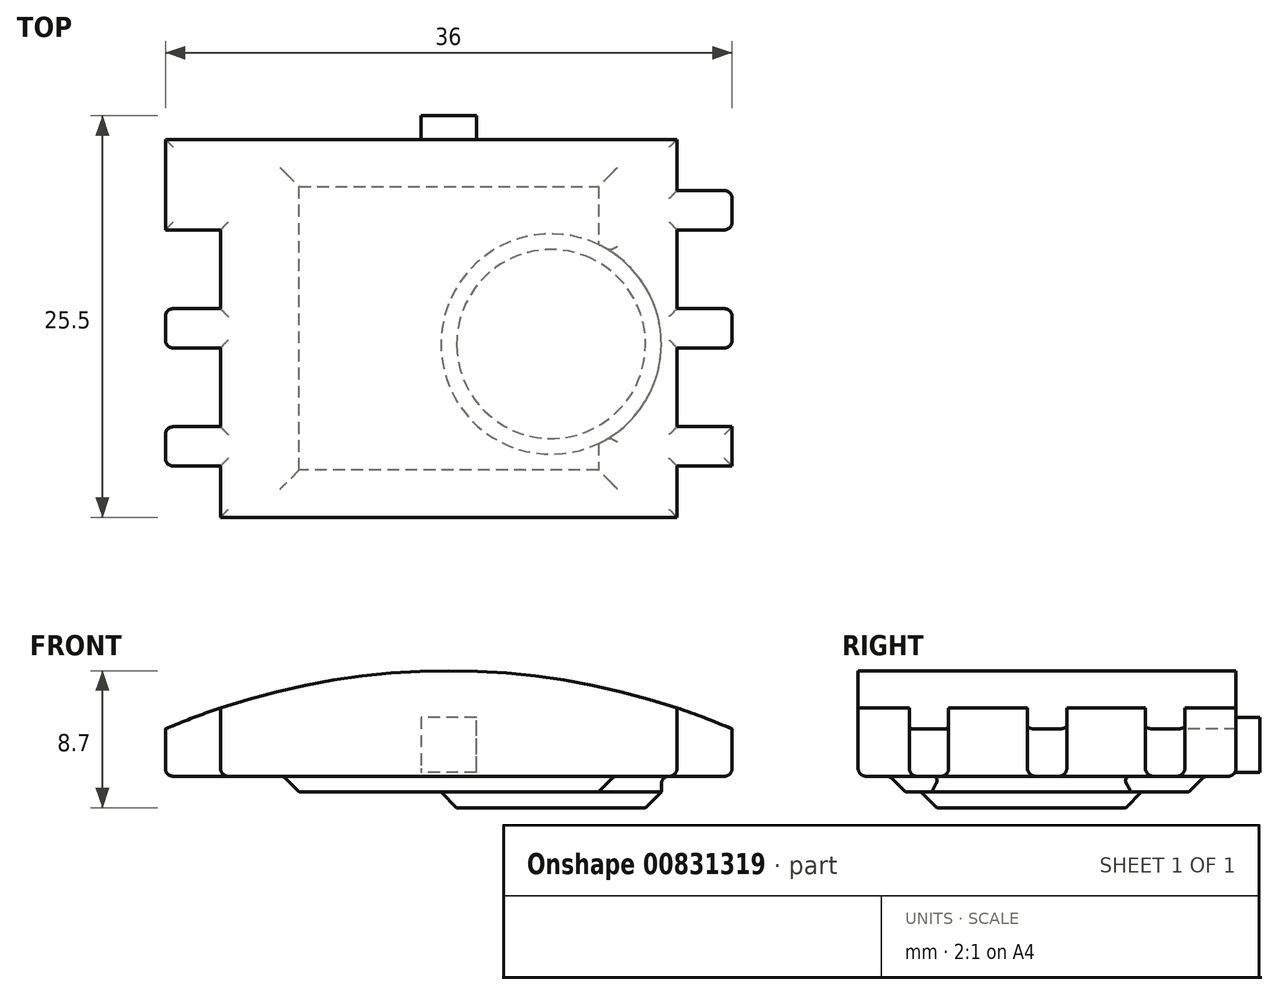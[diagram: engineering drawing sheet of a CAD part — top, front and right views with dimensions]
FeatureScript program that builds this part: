
annotation { "Feature Type Name" : "Feature", "Feature Type Description" : "" }
export const myFeature = defineFeature(function(context is Context, id is Id, definition is map)
    precondition{}
    {
        {
            var Q0;
            Q0=qCreatedBy(makeId("Top.planeOp"),FACE);
            var sketch = newSketch(context, id + "F0", { "sketchPlane" : qUnion([Q0])});
            skLineSegment(sketch, "E0.bottom", {"start": v(18, 12) * mm, "end": v(-18, 12) * mm});
            skLineSegment(sketch, "E0.top", {"start": v(18, -12) * mm, "end": v(-18, -12) * mm});
            skLineSegment(sketch, "E0.left", {"start": v(18, 12) * mm, "end": v(18, -12) * mm});
            skLineSegment(sketch, "E0.right", {"start": v(-18, 12) * mm, "end": v(-18, -12) * mm});
            skPoint(sketch, "E0.middle", {"position": v(0, 0) * mm});
            skSolve(sketch);
        }
        {
            var Q0;
            Q0=makeQuery(id+"F0.imprint","IMPRINT",FACE,{"disambiguationData":[TD([[makeQuery(id+"F0.imprint","IMPRINT",EDGE,{"derivedFrom":sQuery(id+"F0.wireOp",EDGE,"E0.bottom")}),1.0]])]});
            extrude(context, id + "F1", {"entities" : qUnion([Q0]), "depth" : 6.7 * mm, "offsetDistance" : 25 * mm});
        }
        {
            var Q0;
            Q0=makeQuery(id+"F1.opExtrude","SWEPT_FACE",FACE,{"disambiguationData":[OSD([sQuery(id+"F0.wireOp",EDGE,"E0.top")])]});
            var sketch = newSketch(context, id + "F2", { "sketchPlane" : qUnion([Q0])});
            skLineSegment(sketch, "E1", {"start": v(-18, 0) * mm, "end": v(-18, 3) * mm});
            skLineSegment(sketch, "E2.top", {"start": v(-18, 0) * mm, "end": v(18, 0) * mm});
            skLineSegment(sketch, "E2.left", {"start": v(-18, 3) * mm, "end": v(-18, 0) * mm});
            skLineSegment(sketch, "E2.right", {"start": v(18, 4.65) * mm, "end": v(18, 0) * mm});
            skLineSegment(sketch, "E3.bottom", {"start": v(-18, 3) * mm, "end": v(18, 3) * mm});
            skLineSegment(sketch, "E3.right", {"start": v(18, 3) * mm, "end": v(18, 0) * mm});
            skLineSegment(sketch, "E4", {"start": v(0, 3) * mm, "end": v(0, 6.7) * mm});
            skArc(sketch, "E5", {"start": v(18, 3) * mm, "mid": v(0, 6.7) * mm, "end": v(-18, 3) * mm});
            skSolve(sketch);
        }
        {
            var Q0;
            Q0=makeQuery(id+"F2.imprint","IMPRINT",FACE,{"disambiguationData":[TD([[makeQuery(id+"F2.imprint","IMPRINT",EDGE,{"derivedFrom":sQuery(id+"F2.wireOp",EDGE,"E2.top")}),-1.0]])]});
            var Q1;
            {var subQ4=sQuery(id+"F2.wireOp",EDGE,"E4");Q1=makeQuery(id+"F2.imprint","IMPRINT",FACE,{"disambiguationData":[TD([[makeQuery(id+"F2.imprint","IMPRINT",EDGE,{"derivedFrom":subQ4}),1.0]])]});}
            var Q2;
            {var subQ3=sQuery(id+"F2.wireOp",EDGE,"E4");Q2=makeQuery(id+"F2.imprint","IMPRINT",FACE,{"disambiguationData":[TD([[makeQuery(id+"F2.imprint","IMPRINT",EDGE,{"derivedFrom":subQ3}),-1.0]])]});}
            var Q3;
            Q3=makeQuery(id+"F2.imprint","IMPRINT",FACE,{"disambiguationData":[TD([[makeQuery(id+"F2.imprint","IMPRINT",EDGE,{"derivedFrom":sQuery(id+"F2.wireOp",EDGE,"E2.top")}),-1.0]])]});
            extrude(context, id + "F3", {"entities" : qUnion([Q0, Q1, Q2, Q3]), "operationType" : NewBodyOperationType.INTERSECT, "oppositeDirection" : true, "depth" : 50 * mm, "offsetDistance" : 25 * mm});
        }
        {
            var Q0;
            Q0=makeQuery(id+"F1.opExtrude","SWEPT_FACE",FACE,{"disambiguationData":[OSD([sQuery(id+"F0.wireOp",EDGE,"E0.bottom")])]});
            var sketch = newSketch(context, id + "F4", { "sketchPlane" : qUnion([Q0])});
            skLineSegment(sketch, "E6", {"start": v(0, 0) * mm, "end": v(0, 2) * mm});
            skPoint(sketch, "E7.0.midPoint", {"position": v(0, 0) * mm});
            skCircle(sketch, "E8.cCircle", {"center": v(0, 2) * mm, "radius": 1.75 * mm, "construction": true});
            skLineSegment(sketch, "E8.0", {"start": v(1.75, 0.25) * mm, "end": v(-1.75, 0.25) * mm});
            skLineSegment(sketch, "E8.1", {"start": v(-1.75, 0.25) * mm, "end": v(-1.75, 3.75) * mm});
            skLineSegment(sketch, "E8.2", {"start": v(-1.75, 3.75) * mm, "end": v(1.75, 3.75) * mm});
            skLineSegment(sketch, "E8.3", {"start": v(1.75, 3.75) * mm, "end": v(1.75, 0.25) * mm});
            skPoint(sketch, "E8.0.midPoint", {"position": v(0, 0.25) * mm});
            skSolve(sketch);
        }
        {
            var Q0;
            {var subQ0=sQuery(id+"F4.wireOp",EDGE,"E8.1");Q0=makeQuery(id+"F4.imprint","IMPRINT",FACE,{"disambiguationData":[TD([[makeQuery(id+"F4.imprint","IMPRINT",EDGE,{"derivedFrom":subQ0}),-1.0]])]});}
            extrude(context, id + "F5", {"entities" : qUnion([Q0]), "operationType" : NewBodyOperationType.ADD, "depth" : 1.5 * mm, "offsetDistance" : 25 * mm});
        }
        {
            var Q0;
            Q0=makeQuery(id+"F1.opExtrude","CAP_FACE",FACE,{"disambiguationData":[OSD([sQuery(id+"F0.wireOp",EDGE,"E0.bottom"),sQuery(id+"F0.wireOp",EDGE,"E0.top"),sQuery(id+"F0.wireOp",EDGE,"E0.left"),sQuery(id+"F0.wireOp",EDGE,"E0.right")])],"isStart":true});
            var sketch = newSketch(context, id + "F6", { "sketchPlane" : qUnion([Q0])});
            skLineSegment(sketch, "E9.bottom", {"start": v(-10.5, 10) * mm, "end": v(10.5, 10) * mm});
            skLineSegment(sketch, "E9.top", {"start": v(-10.5, -10) * mm, "end": v(10.5, -10) * mm});
            skLineSegment(sketch, "E9.left", {"start": v(-10.5, 10) * mm, "end": v(-10.5, -10) * mm});
            skLineSegment(sketch, "E9.right", {"start": v(10.5, 10) * mm, "end": v(10.5, -10) * mm});
            skLineSegment(sketch, "E10", {"start": v(-18, -12) * mm, "end": v(-18, -8.75) * mm});
            skLineSegment(sketch, "E11", {"start": v(-18, -8.75) * mm, "end": v(-18, -6.25) * mm});
            skLineSegment(sketch, "E12", {"start": v(-18, -6.25) * mm, "end": v(-18, -1.25) * mm});
            skLineSegment(sketch, "E13", {"start": v(-18, -1.25) * mm, "end": v(-18, 1.25) * mm});
            skLineSegment(sketch, "E14", {"start": v(-18, 1.25) * mm, "end": v(-18, 6.25) * mm});
            skLineSegment(sketch, "E15", {"start": v(-18, 6.25) * mm, "end": v(-18, 8.75) * mm});
            skLineSegment(sketch, "E16", {"start": v(-18, 8.75) * mm, "end": v(-18, 12) * mm});
            skLineSegment(sketch, "E17", {"start": v(-18, -12) * mm, "end": v(-14.5, -12) * mm});
            skLineSegment(sketch, "E18.bottom", {"start": v(-14.5, -12) * mm, "end": v(-18, -12) * mm});
            skLineSegment(sketch, "E18.top", {"start": v(-14.5, -8.75) * mm, "end": v(-18, -8.75) * mm});
            skLineSegment(sketch, "E18.left", {"start": v(-14.5, -12) * mm, "end": v(-14.5, -8.75) * mm});
            skLineSegment(sketch, "E19.top", {"start": v(-14.5, -6.25) * mm, "end": v(-18, -6.25) * mm});
            skLineSegment(sketch, "E19.left", {"start": v(-14.5, -8.75) * mm, "end": v(-14.5, -6.25) * mm});
            skLineSegment(sketch, "E20.top", {"start": v(-14.5, -1.25) * mm, "end": v(-18, -1.25) * mm});
            skLineSegment(sketch, "E20.left", {"start": v(-14.5, -6.25) * mm, "end": v(-14.5, -1.25) * mm});
            skLineSegment(sketch, "E21.top", {"start": v(-14.5, 1.25) * mm, "end": v(-18, 1.25) * mm});
            skLineSegment(sketch, "E21.left", {"start": v(-14.5, -1.25) * mm, "end": v(-14.5, 1.25) * mm});
            skLineSegment(sketch, "E22.top", {"start": v(-14.5, 6.25) * mm, "end": v(-18, 6.25) * mm});
            skLineSegment(sketch, "E22.left", {"start": v(-14.5, 1.25) * mm, "end": v(-14.5, 6.25) * mm});
            skLineSegment(sketch, "E23.top", {"start": v(-14.5, 8.75) * mm, "end": v(-18, 8.75) * mm});
            skLineSegment(sketch, "E23.left", {"start": v(-14.5, 6.25) * mm, "end": v(-14.5, 8.75) * mm});
            skLineSegment(sketch, "E24.top", {"start": v(-14.5, 12) * mm, "end": v(-18, 12) * mm});
            skLineSegment(sketch, "E24.left", {"start": v(-14.5, 8.75) * mm, "end": v(-14.5, 12) * mm});
            skLineSegment(sketch, "E25.bottom", {"start": v(18, -12) * mm, "end": v(14.5, -12) * mm});
            skLineSegment(sketch, "E25.top", {"start": v(18, -8.75) * mm, "end": v(14.5, -8.75) * mm});
            skLineSegment(sketch, "E25.left", {"start": v(18, -12) * mm, "end": v(18, -8.75) * mm});
            skLineSegment(sketch, "E25.right", {"start": v(14.5, -12) * mm, "end": v(14.5, -8.75) * mm});
            skLineSegment(sketch, "E26", {"start": v(14.5, -8.75) * mm, "end": v(14.5, -6.25) * mm});
            skLineSegment(sketch, "E27", {"start": v(14.5, -6.25) * mm, "end": v(14.5, -1.25) * mm});
            skLineSegment(sketch, "E28", {"start": v(14.5, -1.25) * mm, "end": v(14.5, 1.25) * mm});
            skLineSegment(sketch, "E29", {"start": v(14.5, 1.25) * mm, "end": v(14.5, 6.25) * mm});
            skLineSegment(sketch, "E30", {"start": v(14.5, 6.25) * mm, "end": v(14.5, 8.75) * mm});
            skLineSegment(sketch, "E31", {"start": v(14.5, 8.75) * mm, "end": v(14.5, 12) * mm});
            skLineSegment(sketch, "E32", {"start": v(14.5, -12) * mm, "end": v(18, -12) * mm});
            skLineSegment(sketch, "E33.top", {"start": v(18, -6.25) * mm, "end": v(14.5, -6.25) * mm});
            skLineSegment(sketch, "E33.left", {"start": v(18, -8.75) * mm, "end": v(18, -6.25) * mm});
            skLineSegment(sketch, "E34.top", {"start": v(18, -1.25) * mm, "end": v(14.5, -1.25) * mm});
            skLineSegment(sketch, "E34.left", {"start": v(18, -6.25) * mm, "end": v(18, -1.25) * mm});
            skLineSegment(sketch, "E35.top", {"start": v(18, 1.25) * mm, "end": v(14.5, 1.25) * mm});
            skLineSegment(sketch, "E35.left", {"start": v(18, -1.25) * mm, "end": v(18, 1.25) * mm});
            skLineSegment(sketch, "E36.top", {"start": v(18, 6.25) * mm, "end": v(14.5, 6.25) * mm});
            skLineSegment(sketch, "E36.left", {"start": v(18, 1.25) * mm, "end": v(18, 6.25) * mm});
            skLineSegment(sketch, "E37.top", {"start": v(18, 8.75) * mm, "end": v(14.5, 8.75) * mm});
            skLineSegment(sketch, "E37.left", {"start": v(18, 6.25) * mm, "end": v(18, 8.75) * mm});
            skLineSegment(sketch, "E38.top", {"start": v(18, 12) * mm, "end": v(14.5, 12) * mm});
            skLineSegment(sketch, "E38.left", {"start": v(18, 8.75) * mm, "end": v(18, 12) * mm});
            skSolve(sketch);
        }
        {
            var Q0;
            Q0=makeQuery(id+"F6.imprint","IMPRINT",FACE,{"disambiguationData":[TD([[makeQuery(id+"F6.imprint","IMPRINT",EDGE,{"derivedFrom":sQuery(id+"F6.wireOp",EDGE,"E9.bottom")}),-1.0]])]});
            extrude(context, id + "F7", {"entities" : qUnion([Q0]), "operationType" : NewBodyOperationType.ADD, "depth" : 1 * mm, "offsetDistance" : 25 * mm});
        }
        {
            var Q0;
            Q0=makeQuery(id+"F7.opExtrude","CAP_EDGE",EDGE,{"disambiguationData":[OSD([sQuery(id+"F6.wireOp",EDGE,"E9.left")])],"isStart":false});
            var Q1;
            Q1=makeQuery(id+"F7.opExtrude","CAP_EDGE",EDGE,{"disambiguationData":[OSD([sQuery(id+"F6.wireOp",EDGE,"E9.bottom")])],"isStart":false});
            var Q2;
            Q2=makeQuery(id+"F7.opExtrude","CAP_EDGE",EDGE,{"disambiguationData":[OSD([sQuery(id+"F6.wireOp",EDGE,"E9.right")])],"isStart":false});
            var Q3;
            Q3=makeQuery(id+"F7.opExtrude","CAP_EDGE",EDGE,{"disambiguationData":[OSD([sQuery(id+"F6.wireOp",EDGE,"E9.top")])],"isStart":false});
            chamfer(context, id + "F8", {"entities" : qUnion([Q0, Q1, Q2, Q3]), "width" : 1 * mm, "tangentPropagation" : true});
        }
        {
            var Q0;
            Q0=makeQuery(id+"F1.opExtrude","CAP_FACE",FACE,{"disambiguationData":[OSD([sQuery(id+"F0.wireOp",EDGE,"E0.bottom"),sQuery(id+"F0.wireOp",EDGE,"E0.top"),sQuery(id+"F0.wireOp",EDGE,"E0.left"),sQuery(id+"F0.wireOp",EDGE,"E0.right")])],"isStart":true});
            var sketch = newSketch(context, id + "F9", { "sketchPlane" : qUnion([Q0])});
            skLineSegment(sketch, "E39.bottom", {"start": v(18, 12) * mm, "end": v(6.5, 12) * mm});
            skLineSegment(sketch, "E39.top", {"start": v(18, 1) * mm, "end": v(6.5, 1) * mm});
            skLineSegment(sketch, "E39.left", {"start": v(18, 12) * mm, "end": v(18, 1) * mm});
            skLineSegment(sketch, "E39.right", {"start": v(6.5, 12) * mm, "end": v(6.5, 1) * mm});
            skCircle(sketch, "E40", {"center": v(6.5, 1) * mm, "radius": 7 * mm});
            skSolve(sketch);
        }
        {
            var Q0;
            {var subQ0=sQuery(id+"F9.wireOp",EDGE,"E39.right");var subQ1=sQuery(id+"F9.wireOp",EDGE,"E39.top");var subQ2=makeQuery(id+"F9.imprint","INTERSECT",VERTEX,{"derivedFrom":[subQ1,subQ0]});Q0=makeQuery(id+"F9.imprint","IMPRINT",FACE,{"disambiguationData":[TD([[makeQuery(id+"F9.imprint","IMPRINT",EDGE,{"disambiguationData":[TD([[subQ2,1.0]])],"derivedFrom":subQ1}),1.0]])]});}
            var Q1;
            {var subQ0=sQuery(id+"F9.wireOp",EDGE,"E39.right");var subQ1=sQuery(id+"F9.wireOp",EDGE,"E39.top");var subQ2=makeQuery(id+"F9.imprint","INTERSECT",VERTEX,{"derivedFrom":[subQ1,subQ0]});Q1=makeQuery(id+"F9.imprint","IMPRINT",FACE,{"disambiguationData":[TD([[makeQuery(id+"F9.imprint","IMPRINT",EDGE,{"disambiguationData":[TD([[subQ2,1.0]])],"derivedFrom":subQ1}),-1.0]])]});}
            var Q2;
            {var subQ0=sQuery(id+"F9.wireOp",EDGE,"E40");var subQ1=sQuery(id+"F9.wireOp",EDGE,"E39.top");var subQ2=makeQuery(id+"F9.imprint","INTERSECT",VERTEX,{"derivedFrom":[subQ1,subQ0]});Q2=makeQuery(id+"F9.imprint","IMPRINT",FACE,{"disambiguationData":[TD([[makeQuery(id+"F9.imprint","IMPRINT",EDGE,{"disambiguationData":[TD([[subQ2,-1.0]])],"derivedFrom":subQ1}),1.0]])]});}
            var Q3;
            {var subQ0=sQuery(id+"F9.wireOp",EDGE,"E40");var subQ1=sQuery(id+"F9.wireOp",EDGE,"E39.top");var subQ2=makeQuery(id+"F9.imprint","INTERSECT",VERTEX,{"derivedFrom":[subQ1,subQ0]});Q3=makeQuery(id+"F9.imprint","IMPRINT",FACE,{"disambiguationData":[TD([[makeQuery(id+"F9.imprint","IMPRINT",EDGE,{"disambiguationData":[TD([[subQ2,-1.0]])],"derivedFrom":subQ1}),-1.0]])]});}
            extrude(context, id + "F10", {"entities" : qUnion([Q0, Q1, Q2, Q3]), "operationType" : NewBodyOperationType.ADD, "depth" : 2 * mm, "offsetDistance" : 25 * mm});
        }
        {
            var Q0;
            Q0=makeQuery(id+"F10.opExtrude","CAP_EDGE",EDGE,{"disambiguationData":[OSD([sQuery(id+"F9.wireOp",EDGE,"E40")])],"isStart":false});
            chamfer(context, id + "F11", {"entities" : qUnion([Q0]), "width" : 1 * mm, "tangentPropagation" : true});
        }
        {
            var Q0;
            Q0=makeQuery(id+"F6.imprint","IMPRINT",FACE,{"disambiguationData":[TD([[makeQuery(id+"F6.imprint","IMPRINT",EDGE,{"derivedFrom":sQuery(id+"F6.wireOp",EDGE,"E37.top")}),-1.0]])]});
            var Q1;
            Q1=makeQuery(id+"F6.imprint","IMPRINT",FACE,{"disambiguationData":[TD([[makeQuery(id+"F6.imprint","IMPRINT",EDGE,{"derivedFrom":sQuery(id+"F6.wireOp",EDGE,"E35.top")}),-1.0]])]});
            var Q2;
            Q2=makeQuery(id+"F6.imprint","IMPRINT",FACE,{"disambiguationData":[TD([[makeQuery(id+"F6.imprint","IMPRINT",EDGE,{"derivedFrom":sQuery(id+"F6.wireOp",EDGE,"E33.top")}),-1.0]])]});
            var Q3;
            Q3=makeQuery(id+"F6.imprint","IMPRINT",FACE,{"disambiguationData":[TD([[makeQuery(id+"F6.imprint","IMPRINT",EDGE,{"derivedFrom":sQuery(id+"F6.wireOp",EDGE,"E25.bottom")}),-1.0]])]});
            var Q4;
            Q4=makeQuery(id+"F6.imprint","IMPRINT",FACE,{"disambiguationData":[TD([[makeQuery(id+"F6.imprint","IMPRINT",EDGE,{"derivedFrom":sQuery(id+"F6.wireOp",EDGE,"E23.top")}),-1.0]])]});
            var Q5;
            Q5=makeQuery(id+"F6.imprint","IMPRINT",FACE,{"disambiguationData":[TD([[makeQuery(id+"F6.imprint","IMPRINT",EDGE,{"derivedFrom":sQuery(id+"F6.wireOp",EDGE,"E21.top")}),-1.0]])]});
            var Q6;
            Q6=makeQuery(id+"F6.imprint","IMPRINT",FACE,{"disambiguationData":[TD([[makeQuery(id+"F6.imprint","IMPRINT",EDGE,{"derivedFrom":sQuery(id+"F6.wireOp",EDGE,"E19.top")}),-1.0]])]});
            var Q7;
            Q7=makeQuery(id+"F6.imprint","IMPRINT",FACE,{"disambiguationData":[TD([[makeQuery(id+"F6.imprint","IMPRINT",EDGE,{"derivedFrom":sQuery(id+"F6.wireOp",EDGE,"E18.bottom")}),-1.0]])]});
            extrude(context, id + "F12", {"entities" : qUnion([Q0, Q1, Q2, Q3, Q4, Q5, Q6, Q7]), "operationType" : NewBodyOperationType.REMOVE, "oppositeDirection" : true, "depth" : 25 * mm, "offsetDistance" : 25 * mm});
        }
        {
            var Q0;
            Q0=makeQuery(id+"F3.boolean.opBoolean","COPY",FACE,{"derivedFrom":makeQuery(id+"F3.boolean.toolComplement.opBoolean","COPY",FACE,{"derivedFrom":makeQuery(id+"F3.opExtrude","SWEPT_FACE",FACE,{"disambiguationData":[OSD([sQuery(id+"F2.wireOp",EDGE,"E5")])]})})});
            var Q1;
            Q1=makeQuery(id+"F12.boolean.opBoolean","COPY",EDGE,{"derivedFrom":makeQuery(id+"F12.opExtrude","SWEPT_EDGE",EDGE,{"disambiguationData":[OSD([sQuery(id+"F0.wireOp",EDGE,"E0.top"),sQuery(id+"F6.wireOp",EDGE,"E24.top"),sQuery(id+"F6.wireOp",EDGE,"E24.left")])]})});
            var Q2;
            Q2=makeQuery(id+"F12.boolean.opBoolean","COPY",EDGE,{"derivedFrom":makeQuery(id+"F12.opExtrude","SWEPT_EDGE",EDGE,{"disambiguationData":[OSD([sQuery(id+"F6.wireOp",EDGE,"E15"),sQuery(id+"F6.wireOp",EDGE,"E23.top"),sQuery(id+"F6.wireOp",EDGE,"E16")])]})});
            var Q3;
            Q3=makeQuery(id+"F12.boolean.opBoolean","COPY",EDGE,{"derivedFrom":makeQuery(id+"F12.opExtrude","SWEPT_EDGE",EDGE,{"disambiguationData":[OSD([sQuery(id+"F6.wireOp",EDGE,"E14"),sQuery(id+"F6.wireOp",EDGE,"E22.top"),sQuery(id+"F6.wireOp",EDGE,"E15")])]})});
            var Q4;
            Q4=makeQuery(id+"F12.boolean.opBoolean","COPY",EDGE,{"derivedFrom":makeQuery(id+"F12.opExtrude","SWEPT_EDGE",EDGE,{"disambiguationData":[OSD([sQuery(id+"F6.wireOp",EDGE,"E13"),sQuery(id+"F6.wireOp",EDGE,"E21.top"),sQuery(id+"F6.wireOp",EDGE,"E14")])]})});
            var Q5;
            Q5=makeQuery(id+"F12.boolean.opBoolean","COPY",EDGE,{"derivedFrom":makeQuery(id+"F12.opExtrude","SWEPT_EDGE",EDGE,{"disambiguationData":[OSD([sQuery(id+"F6.wireOp",EDGE,"E12"),sQuery(id+"F6.wireOp",EDGE,"E20.top"),sQuery(id+"F6.wireOp",EDGE,"E13")])]})});
            var Q6;
            Q6=makeQuery(id+"F12.boolean.opBoolean","COPY",EDGE,{"derivedFrom":makeQuery(id+"F12.opExtrude","SWEPT_EDGE",EDGE,{"disambiguationData":[OSD([sQuery(id+"F6.wireOp",EDGE,"E10"),sQuery(id+"F6.wireOp",EDGE,"E18.top"),sQuery(id+"F6.wireOp",EDGE,"E11")])]})});
            var Q7;
            Q7=makeQuery(id+"F12.boolean.opBoolean","COPY",EDGE,{"derivedFrom":makeQuery(id+"F12.opExtrude","SWEPT_EDGE",EDGE,{"disambiguationData":[OSD([sQuery(id+"F6.wireOp",EDGE,"E11"),sQuery(id+"F6.wireOp",EDGE,"E19.top"),sQuery(id+"F6.wireOp",EDGE,"E12")])]})});
            var Q8;
            Q8=makeQuery(id+"F12.boolean.opBoolean","COPY",EDGE,{"derivedFrom":makeQuery(id+"F12.opExtrude","SWEPT_EDGE",EDGE,{"disambiguationData":[OSD([sQuery(id+"F0.wireOp",EDGE,"E0.bottom"),sQuery(id+"F6.wireOp",EDGE,"E18.bottom"),sQuery(id+"F6.wireOp",EDGE,"E18.left")])]})});
            var Q9;
            Q9=makeQuery(id+"F12.boolean.opBoolean","COPY",EDGE,{"derivedFrom":makeQuery(id+"F12.opExtrude","SWEPT_EDGE",EDGE,{"disambiguationData":[OSD([sQuery(id+"F6.wireOp",EDGE,"E35.left"),sQuery(id+"F6.wireOp",EDGE,"E35.top"),sQuery(id+"F6.wireOp",EDGE,"E36.left")])]})});
            var Q10;
            Q10=makeQuery(id+"F12.boolean.opBoolean","COPY",EDGE,{"derivedFrom":makeQuery(id+"F12.opExtrude","SWEPT_EDGE",EDGE,{"disambiguationData":[OSD([sQuery(id+"F6.wireOp",EDGE,"E34.left"),sQuery(id+"F6.wireOp",EDGE,"E34.top"),sQuery(id+"F6.wireOp",EDGE,"E35.left")])]})});
            var Q11;
            Q11=makeQuery(id+"F12.boolean.opBoolean","COPY",EDGE,{"derivedFrom":makeQuery(id+"F12.opExtrude","SWEPT_EDGE",EDGE,{"disambiguationData":[OSD([sQuery(id+"F6.wireOp",EDGE,"E33.left"),sQuery(id+"F6.wireOp",EDGE,"E33.top"),sQuery(id+"F6.wireOp",EDGE,"E34.left")])]})});
            var Q12;
            Q12=makeQuery(id+"F12.boolean.opBoolean","COPY",EDGE,{"derivedFrom":makeQuery(id+"F12.opExtrude","SWEPT_EDGE",EDGE,{"disambiguationData":[OSD([sQuery(id+"F6.wireOp",EDGE,"E25.left"),sQuery(id+"F6.wireOp",EDGE,"E25.top"),sQuery(id+"F6.wireOp",EDGE,"E33.left")])]})});
            var Q13;
            Q13=makeQuery(id+"F12.boolean.opBoolean","COPY",EDGE,{"derivedFrom":makeQuery(id+"F12.opExtrude","SWEPT_EDGE",EDGE,{"disambiguationData":[OSD([sQuery(id+"F0.wireOp",EDGE,"E0.bottom"),sQuery(id+"F6.wireOp",EDGE,"E25.bottom"),sQuery(id+"F6.wireOp",EDGE,"E25.right")])]})});
            var Q14;
            Q14=makeQuery(id+"F12.boolean.opBoolean","COPY",EDGE,{"derivedFrom":makeQuery(id+"F12.opExtrude","SWEPT_EDGE",EDGE,{"disambiguationData":[OSD([sQuery(id+"F6.wireOp",EDGE,"E36.left"),sQuery(id+"F6.wireOp",EDGE,"E36.top"),sQuery(id+"F6.wireOp",EDGE,"E37.left")])]})});
            var Q15;
            Q15=makeQuery(id+"F12.boolean.opBoolean","COPY",EDGE,{"derivedFrom":makeQuery(id+"F12.opExtrude","SWEPT_EDGE",EDGE,{"disambiguationData":[OSD([sQuery(id+"F6.wireOp",EDGE,"E37.left"),sQuery(id+"F6.wireOp",EDGE,"E37.top"),sQuery(id+"F6.wireOp",EDGE,"E38.left")])]})});
            var Q16;
            Q16=makeQuery(id+"F12.boolean.opBoolean","COPY",EDGE,{"derivedFrom":makeQuery(id+"F12.opExtrude","SWEPT_EDGE",EDGE,{"disambiguationData":[OSD([sQuery(id+"F0.wireOp",EDGE,"E0.top"),sQuery(id+"F6.wireOp",EDGE,"E38.top"),sQuery(id+"F6.wireOp",EDGE,"E31")])]})});
            var Q17;
            Q17=makeQuery(id+"F1.opExtrude","CAP_FACE",FACE,{"disambiguationData":[OSD([sQuery(id+"F0.wireOp",EDGE,"E0.bottom"),sQuery(id+"F0.wireOp",EDGE,"E0.top"),sQuery(id+"F0.wireOp",EDGE,"E0.left"),sQuery(id+"F0.wireOp",EDGE,"E0.right")])],"isStart":true});
            fillet(context, id + "F13", {"entities" : qUnion([Q0, Q1, Q2, Q3, Q4, Q5, Q6, Q7, Q8, Q9, Q10, Q11, Q12, Q13, Q14, Q15, Q16, Q17]), "radius" : .5 * mm, "tangentPropagation" : true, "allowEdgeOverflow" : false});
        }
    });
